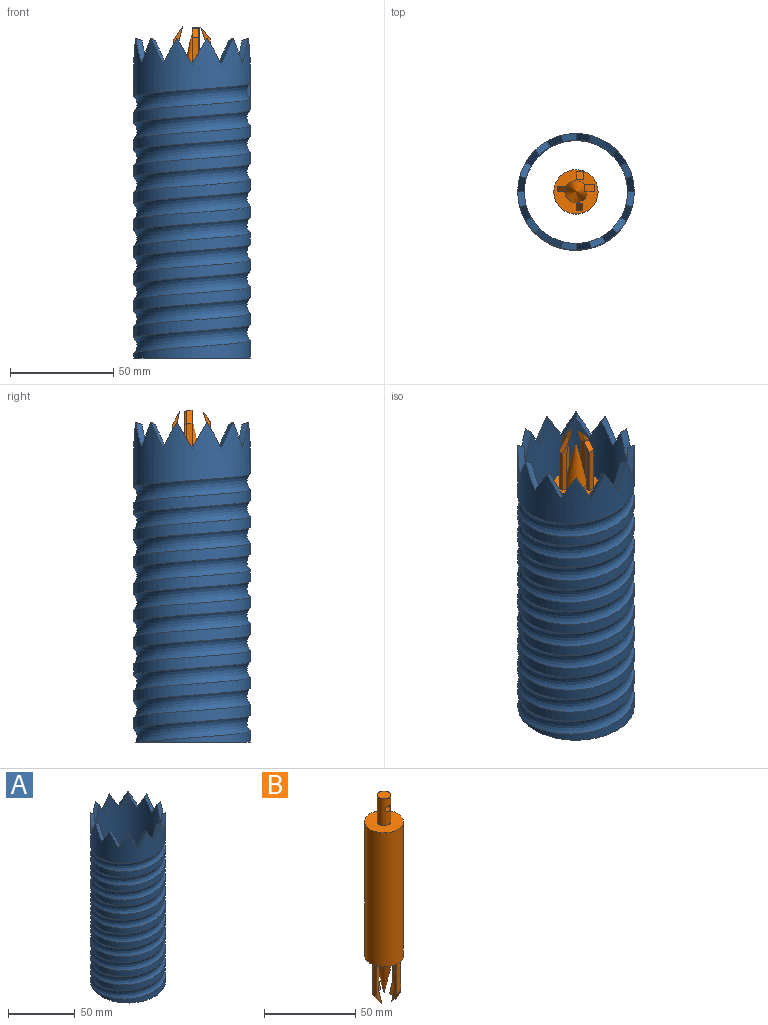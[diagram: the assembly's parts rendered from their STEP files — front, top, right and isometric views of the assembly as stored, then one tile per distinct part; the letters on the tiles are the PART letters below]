
ASSEMBLY  parts=2 mates=1
PART A: 52 faces, bbox 64.9x64.9x162 mm
  f0: cylinder r=28.17mm len=56.34mm, axis (0,0,1), area 3908.9mm2, adj f1,f11,f12,f14,f15,f16,f17,f18
  f1: cylinder r=28.17mm len=56.34mm, axis (0,0,1), area 960.4mm2, adj f0,f2,f37
  f2: cylinder r=28.17mm len=56.34mm, axis (0,0,1), area 960.1mm2, adj f1,f3,f37
  f3: cylinder r=28.17mm len=56.34mm, axis (0,0,1), area 959.7mm2, adj f2,f4,f37
  f4: cylinder r=28.17mm len=56.34mm, axis (0,0,1), area 959.5mm2, adj f3,f5,f37
  f5: cylinder r=28.17mm len=56.34mm, axis (0,0,1), area 959.8mm2, adj f4,f6,f37
  f6: cylinder r=28.17mm len=56.34mm, axis (0,0,1), area 960.1mm2, adj f5,f7,f37
  f7: cylinder r=28.17mm len=56.34mm, axis (0,0,1), area 959.9mm2, adj f6,f8,f37
  f8: cylinder r=28.17mm len=56.34mm, axis (0,0,1), area 959.6mm2, adj f7,f9,f37
  f9: cylinder r=28.17mm len=56.34mm, axis (0,0,1), area 959.5mm2, adj f8,f10,f37
  f10: cylinder r=28.17mm len=56.34mm, axis (0,0,1), area 504.7mm2, adj f9,f36,f37,f38
  f11: plane 0.11x0.06mm, normal (0,0,1), area 0mm2, adj f0,f14,f50
  f12: plane 0.1x0.1mm, normal (0,0,1), area 0mm2, adj f0,f15,f51
  f13: cylinder r=25mm len=153.63mm, axis (0,0,1), area 23251.6mm2, adj f14,f15,f17,f19,f21,f23,f25,f27
  f14: plane 12.68x7.36mm, normal (-0.87,0,0.5), area 44.1mm2, adj f0,f11,f13,f35,f50
  f15: plane 12.68x7.5mm, normal (0.43,-0.75,0.5), area 44.1mm2, adj f0,f12,f13,f49,f51
  f16: plane 0.11x0.06mm, normal (0,0,1), area 0mm2, adj f0,f17,f49
  f17: plane 12.68x7.36mm, normal (0,-0.87,0.5), area 44.1mm2, adj f0,f13,f16,f48,f49
  f18: plane 0.11x0.06mm, normal (0,0,1), area 0mm2, adj f0,f19,f48
  f19: plane 12.68x7.71mm, normal (-0.43,-0.75,0.5), area 44.1mm2, adj f0,f13,f18,f47,f48
  f20: plane 0.1x0.1mm, normal (0,0,1), area 0mm2, adj f0,f21,f47
  f21: plane 12.68x7.5mm, normal (-0.75,-0.43,0.5), area 44.1mm2, adj f0,f13,f20,f46,f47
  f22: plane 0.11x0.06mm, normal (0,0,1), area 0mm2, adj f0,f23,f46
  f23: plane 12.68x7.36mm, normal (-0.87,0,0.5), area 44.1mm2, adj f0,f13,f22,f45,f46
  f24: plane 0.11x0.06mm, normal (0,0,1), area 0mm2, adj f0,f25,f45
  f25: plane 12.68x7.71mm, normal (-0.75,0.43,0.5), area 44.1mm2, adj f0,f13,f24,f44,f45
  f26: plane 0.1x0.1mm, normal (0,0,1), area 0mm2, adj f0,f27,f44
  f27: plane 12.68x7.5mm, normal (-0.43,0.75,0.5), area 44.1mm2, adj f0,f13,f26,f43,f44
  f28: plane 0.11x0.06mm, normal (0,0,1), area 0mm2, adj f0,f29,f43
  f29: plane 12.68x7.36mm, normal (0,0.87,0.5), area 44.1mm2, adj f0,f13,f28,f42,f43
  f30: plane 0.11x0.06mm, normal (0,0,1), area 0mm2, adj f0,f31,f42
  f31: plane 12.68x7.71mm, normal (0.43,0.75,0.5), area 44.1mm2, adj f0,f13,f30,f41,f42
  f32: plane 0.1x0.1mm, normal (0,0,1), area 0mm2, adj f0,f33,f41
  f33: plane 12.68x7.5mm, normal (0.75,0.43,0.5), area 44.1mm2, adj f0,f13,f32,f40,f41
  f34: plane 0.11x0.06mm, normal (0,0,1), area 0mm2, adj f0,f35,f40
  f35: plane 12.68x7.36mm, normal (0.87,0,0.5), area 44.1mm2, adj f0,f13,f14,f34,f40
  f36: plane 57.44x56.59mm, normal (0,0,-1), area 461.6mm2, adj f10,f13,f37,f38
  f37: bspline ~140.66x63.84mm, area 14228.3mm2, adj f0,f1,f2,f3,f4,f5,f6,f7
  f38: plane 3.33x1.69mm, normal (0,1,0), area 3.2mm2, adj f10,f36,f37
  f39: plane 7.75x1.75mm, normal (0,-1,0), area 8.2mm2, adj f0,f37
  f40: plane 12.68x7.71mm, normal (-0.75,-0.43,0.5), area 44.1mm2, adj f0,f13,f33,f34,f35
  f41: plane 12.68x7.5mm, normal (-0.43,-0.75,0.5), area 44.1mm2, adj f0,f13,f31,f32,f33
  f42: plane 12.68x7.36mm, normal (0,-0.87,0.5), area 44.1mm2, adj f0,f13,f29,f30,f31
  f43: plane 12.68x7.71mm, normal (0.43,-0.75,0.5), area 44.1mm2, adj f0,f13,f27,f28,f29
  f44: plane 12.68x7.5mm, normal (0.75,-0.43,0.5), area 44.1mm2, adj f0,f13,f25,f26,f27
  f45: plane 12.68x7.36mm, normal (0.87,0,0.5), area 44.1mm2, adj f0,f13,f23,f24,f25
  f46: plane 12.68x7.71mm, normal (0.75,0.43,0.5), area 44.1mm2, adj f0,f13,f21,f22,f23
  f47: plane 12.68x7.5mm, normal (0.43,0.75,0.5), area 44.1mm2, adj f0,f13,f19,f20,f21
  f48: plane 12.68x7.36mm, normal (0,0.87,0.5), area 44.1mm2, adj f0,f13,f17,f18,f19
  f49: plane 12.68x7.71mm, normal (-0.43,0.75,0.5), area 44.1mm2, adj f0,f13,f15,f16,f17
  f50: plane 12.68x7.71mm, normal (0.75,-0.43,0.5), area 44.1mm2, adj f0,f11,f13,f14,f51
  f51: plane 12.68x7.5mm, normal (-0.75,0.43,0.5), area 44.1mm2, adj f0,f12,f13,f15,f50
PART B: 31 faces, bbox 21.4x21.4x136.2 mm
  f0: plane 21.38x21.38mm, normal (0,0,1), area 315.1mm2, adj f3,f28
  f1: cone r=0mm half-angle=12.1deg, axis (0,0,1), area 429.3mm2, adj f2
  f2: plane 21.38x21.38mm, normal (0,0,-1), area 242.7mm2, adj f1,f3,f4,f7,f8,f9,f10,f11
  f3: cylinder r=10.69mm len=90mm, axis (0,0,1), area 6045.4mm2, adj f0,f2
  f4: plane 21.81x2.7mm, normal (-1,0,0), area 58.9mm2, adj f2,f5,f8,f9
  f5: plane 6.46x4.41mm, normal (-0.83,0,-0.56), area 21.1mm2, adj f4,f6,f8,f9
  f6: plane 9.08x2.7mm, normal (0.97,0,0.24), area 25.2mm2, adj f5,f7,f8,f9
  f7: plane 19.19x2.7mm, normal (1,0,-0.01), area 51.8mm2, adj f2,f6,f8,f9
  f8: plane 28.26x4.41mm, normal (0,-1,0), area 60mm2, adj f2,f4,f5,f6,f7
  f9: plane 28.26x4.41mm, normal (0,1,0), area 60mm2, adj f2,f4,f5,f6,f7
  f10: plane 21.97x3.4mm, normal (1,0,0), area 74.7mm2, adj f2,f13,f14,f15
  f11: plane 21.01x3.4mm, normal (-1,0,0), area 71.4mm2, adj f2,f12,f14,f15
  f12: plane 6.73x3.4mm, normal (-0.96,0,0.29), area 23.9mm2, adj f11,f13,f14,f15
  f13: plane 5.77x4.49mm, normal (0.79,0,-0.61), area 24.9mm2, adj f10,f12,f14,f15
  f14: plane 27.74x4.49mm, normal (0,-1,0), area 62.1mm2, adj f2,f10,f11,f12,f13
  f15: plane 27.74x4.49mm, normal (0,1,0), area 62.1mm2, adj f2,f10,f11,f12,f13
  f16: plane 20.81x3.4mm, normal (0,-1,0), area 70.7mm2, adj f2,f17,f20,f21
  f17: plane 6.72x3.6mm, normal (0,-0.88,-0.47), area 25.9mm2, adj f16,f18,f20,f21
  f18: plane 8.31x3.4mm, normal (0,0.98,0.21), area 28.9mm2, adj f17,f19,f20,f21
  f19: plane 19.21x3.4mm, normal (0,1,0), area 65.3mm2, adj f2,f18,f20,f21
  f20: plane 27.53x3.6mm, normal (1,0,0), area 44.9mm2, adj f2,f16,f17,f18,f19
  f21: plane 27.53x3.6mm, normal (-1,0,0), area 44.9mm2, adj f2,f16,f17,f18,f19
  f22: plane 22.73x3.1mm, normal (0,1,0), area 70.5mm2, adj f2,f25,f26,f27
  f23: plane 21.13x3.1mm, normal (0,-1,0), area 65.5mm2, adj f2,f24,f26,f27
  f24: plane 5.88x3.1mm, normal (0,-0.96,0.3), area 19.1mm2, adj f23,f25,f26,f27
  f25: plane 4.27x3.63mm, normal (0,0.76,-0.65), area 17.4mm2, adj f22,f24,f26,f27
  f26: plane 27.01x3.63mm, normal (1,0,0), area 46.6mm2, adj f2,f22,f23,f24,f25
  f27: plane 27.01x3.63mm, normal (-1,0,0), area 46.6mm2, adj f2,f22,f23,f24,f25
  f28: cylinder r=3.74mm len=17.9mm, axis (0,0,-1), area 394.3mm2, adj f0,f29,f30
  f29: plane 7.48x7.48mm, normal (0,0,1), area 43.9mm2, adj f28
  f30: cylinder r=2mm len=7.48mm, axis (0,-1,0), area 86.9mm2, adj f28
PLACE A t=(155.82,253.32,-131.49)mm fixed
PLACE B rot(axis=(1,0,0),180deg) t=(155.82,253.32,-109.18)mm
MATE slider B.f1 <-> A.f13  axis (0,0,-1) through (155.82,253.32,-142.38)mm
